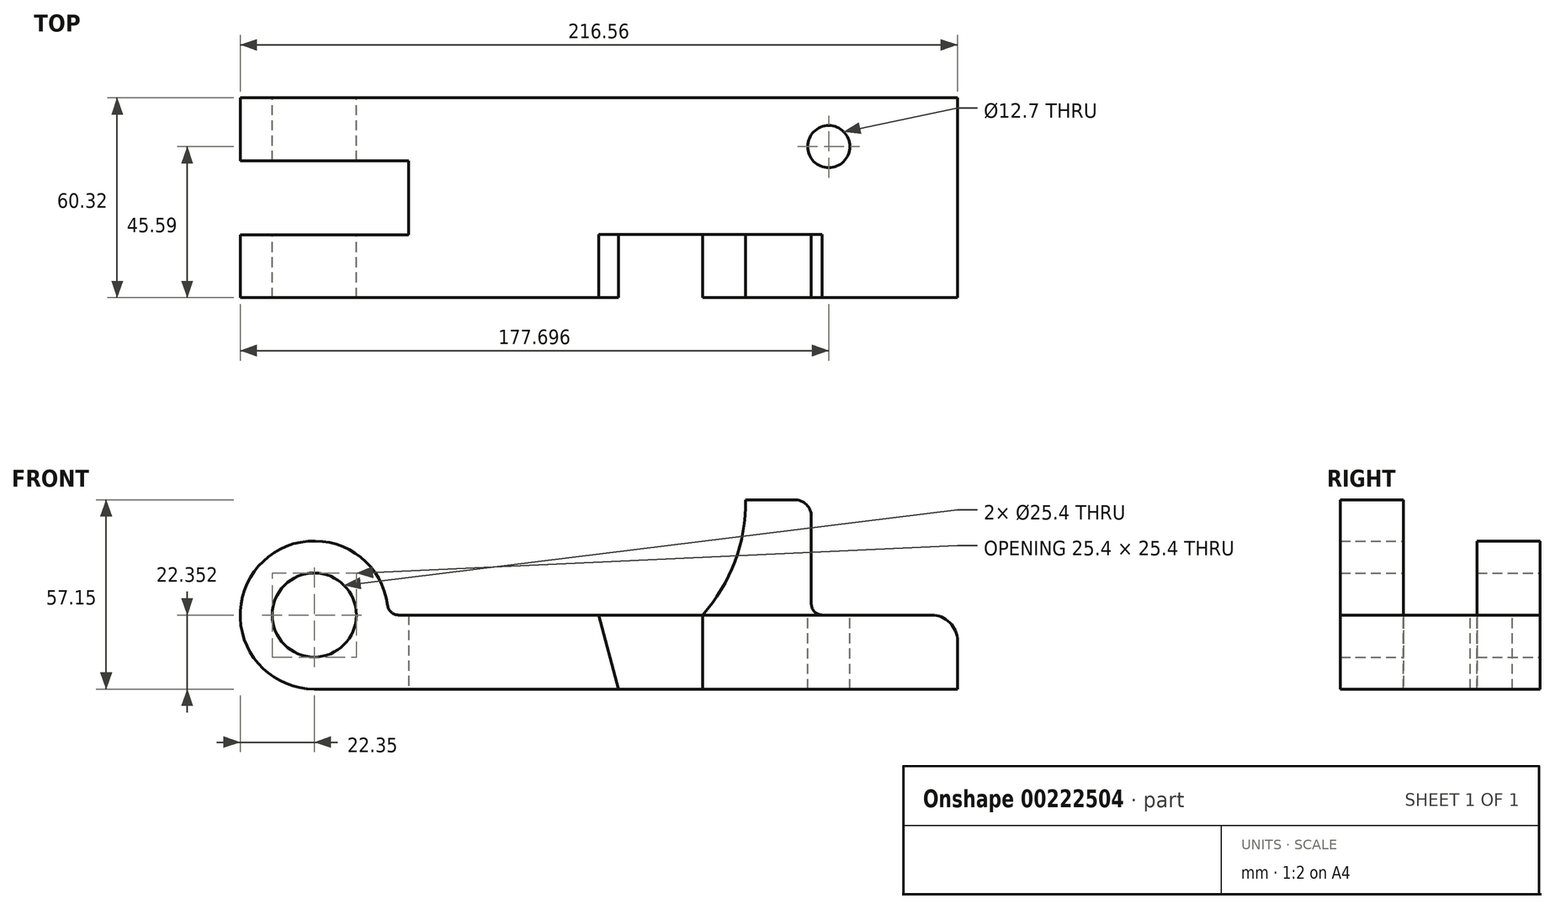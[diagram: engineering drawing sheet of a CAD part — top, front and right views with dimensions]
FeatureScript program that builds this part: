
annotation { "Feature Type Name" : "Feature", "Feature Type Description" : "" }
export const myFeature = defineFeature(function(context is Context, id is Id, definition is map)
    precondition{}
    {
        {
            var Q0;
            Q0=qCreatedBy(makeId("Front.planeOp"),FACE);
            var sketch = newSketch(context, id + "F0", { "sketchPlane" : qUnion([Q0])});
            skLineSegment(sketch, "E0", {"start": v(0, 0) * mm, "end": v(194.2, 0) * mm});
            skLineSegment(sketch, "E1", {"start": v(0, 0) * mm, "end": v(0, 44.7) * mm, "construction": true});
            skArc(sketch, "E2", {"start": v(22.35, 22.35) * mm, "mid": v(-15.8, 38.16) * mm, "end": v(0, 0) * mm});
            skCircle(sketch, "E3", {"center": v(0, 22.35) * mm, "radius": 12.7 * mm});
            skLineSegment(sketch, "E4", {"start": v(194.2, 0) * mm, "end": v(194.2, 22.35) * mm});
            skLineSegment(sketch, "E5", {"start": v(194.2, 22.35) * mm, "end": v(22.35, 22.35) * mm});
            skSolve(sketch);
        }
        {
            var Q0;
            Q0=makeQuery(id+"F0.imprint","IMPRINT",FACE,{"disambiguationData":[TD([[makeQuery(id+"F0.imprint","IMPRINT",EDGE,{"derivedFrom":sQuery(id+"F0.wireOp",EDGE,"E0")}),1.0]])]});
            extrude(context, id + "F1", {"entities" : qUnion([Q0]), "endBound" : BoundingType.SYMMETRIC, "depth" : 60.32 * mm});
        }
        {
            var Q0;
            Q0=qCreatedBy(makeId("Top.planeOp"),FACE);
            var sketch = newSketch(context, id + "F2", { "sketchPlane" : qUnion([Q0])});
            skLineSegment(sketch, "E6.bottom", {"start": v(-28.46, 11.16) * mm, "end": v(28.46, 11.16) * mm});
            skLineSegment(sketch, "E6.top", {"start": v(-28.46, -11.16) * mm, "end": v(28.46, -11.16) * mm});
            skLineSegment(sketch, "E6.left", {"start": v(-28.46, 11.16) * mm, "end": v(-28.46, -11.16) * mm});
            skLineSegment(sketch, "E6.right", {"start": v(28.46, 11.16) * mm, "end": v(28.46, -11.16) * mm});
            skPoint(sketch, "E6.middle", {"position": v(0, 0) * mm});
            skSolve(sketch);
        }
        {
            var Q0;
            Q0=makeQuery(id+"F2.imprint","IMPRINT",FACE,{"disambiguationData":[TD([[makeQuery(id+"F2.imprint","IMPRINT",EDGE,{"derivedFrom":sQuery(id+"F2.wireOp",EDGE,"E6.bottom")}),-1.0]])]});
            extrude(context, id + "F3", {"entities" : qUnion([Q0]), "operationType" : NewBodyOperationType.REMOVE, "endBound" : BoundingType.THROUGH_ALL, "depth" : 25.4 * mm});
        }
        {
            var Q0;
            {var subQ0=sQuery(id+"F0.wireOp",EDGE,"E5");var subQ1=sQuery(id+"F0.wireOp",EDGE,"E2");Q0=makeQuery(id+"F3.boolean.opBoolean","SPLIT",EDGE,{"disambiguationData":[TD([makeQuery(id+"F3.opExtrude","SWEPT_FACE",FACE,{"disambiguationData":[OSD([sQuery(id+"F2.wireOp",EDGE,"E6.bottom")])]})])],"derivedFrom":makeQuery(id+"F1.opExtrude","SWEPT_EDGE",EDGE,{"disambiguationData":[OSD([subQ1,subQ0])]})});}
            fillet(context, id + "F4", {"entities" : qUnion([Q0]), "radius" : 3.3 * mm, "tangentPropagation" : true, "allowEdgeOverflow" : false});
        }
        {
            var Q0;
            {var subQ0=sQuery(id+"F0.wireOp",EDGE,"E5");var subQ1=sQuery(id+"F0.wireOp",EDGE,"E2");Q0=makeQuery(id+"F3.boolean.opBoolean","SPLIT",EDGE,{"disambiguationData":[TD([makeQuery(id+"F3.opExtrude","SWEPT_FACE",FACE,{"disambiguationData":[OSD([sQuery(id+"F2.wireOp",EDGE,"E6.top")])]})])],"derivedFrom":makeQuery(id+"F1.opExtrude","SWEPT_EDGE",EDGE,{"disambiguationData":[OSD([subQ1,subQ0])]})});}
            fillet(context, id + "F5", {"entities" : qUnion([Q0]), "radius" : 3.3 * mm, "tangentPropagation" : true, "allowEdgeOverflow" : false});
        }
        {
            var Q0;
            Q0=makeQuery(id+"F1.opExtrude","SWEPT_FACE",FACE,{"disambiguationData":[OSD([sQuery(id+"F0.wireOp",EDGE,"E5")])]});
            var sketch = newSketch(context, id + "F6", { "sketchPlane" : qUnion([Q0])});
            skCircle(sketch, "E7", {"center": v(155.35, 15.43) * mm, "radius": 6.35 * mm});
            skSolve(sketch);
        }
        {
            var Q0;
            Q0=makeQuery(id+"F6.imprint","IMPRINT",FACE,{"disambiguationData":[TD([[makeQuery(id+"F6.imprint","IMPRINT",EDGE,{"derivedFrom":sQuery(id+"F6.wireOp",EDGE,"E7")}),1.0]])]});
            extrude(context, id + "F7", {"entities" : qUnion([Q0]), "operationType" : NewBodyOperationType.REMOVE, "endBound" : BoundingType.THROUGH_ALL, "oppositeDirection" : true, "depth" : 25.4 * mm});
        }
        {
            var Q0;
            Q0=makeQuery(id+"F1.opExtrude","CAP_FACE",FACE,{"disambiguationData":[OSD([sQuery(id+"F0.wireOp",EDGE,"E0"),sQuery(id+"F0.wireOp",EDGE,"E2"),sQuery(id+"F0.wireOp",EDGE,"E3"),sQuery(id+"F0.wireOp",EDGE,"E4"),sQuery(id+"F0.wireOp",EDGE,"E5")])],"isStart":false});
            var sketch = newSketch(context, id + "F8", { "sketchPlane" : qUnion([Q0])});
            skLineSegment(sketch, "E8", {"start": v(117.25, 22.35) * mm, "end": v(117.25, 0) * mm});
            skLineSegment(sketch, "E9", {"start": v(117.25, 0) * mm, "end": v(91.85, 0) * mm});
            skLineSegment(sketch, "E10", {"start": v(91.85, 0) * mm, "end": v(85.85, 22.35) * mm});
            skLineSegment(sketch, "E11", {"start": v(85.85, 22.35) * mm, "end": v(117.25, 22.35) * mm});
            skSolve(sketch);
        }
        {
            var Q0;
            Q0=makeQuery(id+"F8.imprint","IMPRINT",FACE,{"disambiguationData":[TD([[makeQuery(id+"F8.imprint","IMPRINT",EDGE,{"derivedFrom":sQuery(id+"F8.wireOp",EDGE,"E8")}),-1.0]])]});
            extrude(context, id + "F9", {"entities" : qUnion([Q0]), "operationType" : NewBodyOperationType.REMOVE, "oppositeDirection" : true, "depth" : 19.05 * mm});
        }
        {
            var Q0;
            {var subQ0=sQuery(id+"F0.wireOp",EDGE,"E0");var subQ1=sQuery(id+"F0.wireOp",EDGE,"E4");var subQ2=sQuery(id+"F0.wireOp",EDGE,"E5");Q0=makeQuery(id+"F9.boolean.opBoolean","SPLIT",FACE,{"disambiguationData":[TD([makeQuery(id+"F1.opExtrude","SWEPT_FACE",FACE,{"disambiguationData":[OSD([subQ1])]})])],"derivedFrom":makeQuery(id+"F1.opExtrude","CAP_FACE",FACE,{"disambiguationData":[OSD([subQ0,sQuery(id+"F0.wireOp",EDGE,"E2"),sQuery(id+"F0.wireOp",EDGE,"E3"),subQ1,subQ2])],"isStart":false})});}
            var sketch = newSketch(context, id + "F10", { "sketchPlane" : qUnion([Q0])});
            skLineSegment(sketch, "E12.bottom", {"start": v(117.25, 22.35) * mm, "end": v(150.09, 22.35) * mm});
            skLineSegment(sketch, "E12.top", {"start": v(130.2, 57.15) * mm, "end": v(150.09, 57.15) * mm});
            skLineSegment(sketch, "E12.right", {"start": v(150.09, 25.65) * mm, "end": v(150.09, 57.15) * mm});
            skArc(sketch, "E13", {"start": v(117.25, 22.35) * mm, "mid": v(127.01, 38.53) * mm, "end": v(130.2, 57.15) * mm});
            skLineSegment(sketch, "E14", {"start": v(150.09, 22.35) * mm, "end": v(153.4, 22.35) * mm});
            skArc(sketch, "E15", {"start": v(150.09, 25.65) * mm, "mid": v(151.06, 23.32) * mm, "end": v(153.4, 22.35) * mm});
            skSolve(sketch);
        }
        {
            var Q0;
            Q0=makeQuery(id+"F10.imprint","IMPRINT",FACE,{"disambiguationData":[TD([[makeQuery(id+"F10.imprint","IMPRINT",EDGE,{"derivedFrom":sQuery(id+"F10.wireOp",EDGE,"E12.bottom")}),-1.0]])]});
            extrude(context, id + "F11", {"entities" : qUnion([Q0]), "oppositeDirection" : true, "depth" : 19.05 * mm});
        }
        {
            var Q0;
            Q0=makeQuery(id+"F1.opExtrude","SWEPT_EDGE",EDGE,{"disambiguationData":[OSD([sQuery(id+"F0.wireOp",EDGE,"E4"),sQuery(id+"F0.wireOp",EDGE,"E5")])]});
            fillet(context, id + "F12", {"entities" : qUnion([Q0]), "radius" : 7.87 * mm, "tangentPropagation" : true, "allowEdgeOverflow" : false});
        }
        {
            var Q0;
            Q0=makeQuery(id+"F11.opExtrude","SWEPT_EDGE",EDGE,{"disambiguationData":[OSD([sQuery(id+"F10.wireOp",EDGE,"E12.top"),sQuery(id+"F10.wireOp",EDGE,"E12.right")])]});
            fillet(context, id + "F13", {"entities" : qUnion([Q0]), "radius" : 5.08 * mm, "tangentPropagation" : true, "allowEdgeOverflow" : false});
        }
    });
